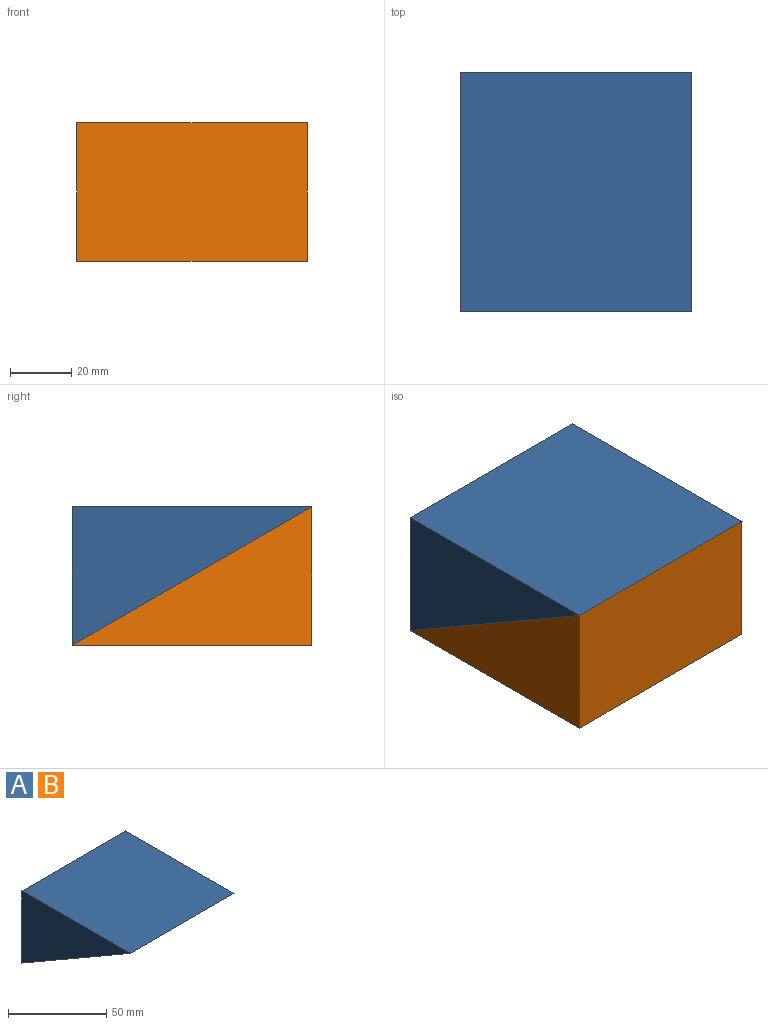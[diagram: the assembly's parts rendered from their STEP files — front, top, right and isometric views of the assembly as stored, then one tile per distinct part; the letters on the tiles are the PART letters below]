
ASSEMBLY  parts=2 mates=1
PART A: 5 faces, bbox 75x77.9x45 mm
  f0: plane 77.94x75mm, normal (0,0,1), area 5845.7mm2, adj f1,f2,f3,f4
  f1: plane 77.94x75mm, normal (0,-0.5,-0.87), area 6750mm2, adj f0,f2,f3,f4
  f2: plane 75x45mm, normal (0,1,0), area 3375mm2, adj f0,f1,f3,f4
  f3: plane 77.94x45mm, normal (1,0,0), area 1753.7mm2, adj f0,f1,f2
  f4: plane 77.94x45mm, normal (-1,0,0), area 1753.7mm2, adj f0,f1,f2
PART B: same geometry as A
PLACE A t=(218.29,-49.33,-132.39)mm
PLACE B rot(axis=(1,0,0),180deg) t=(218.29,28.61,-177.39)mm
MATE revolute B.f1 <-> A.f1  axis (0,0.5,0.87) through (218.29,-10.36,-154.89)mm
